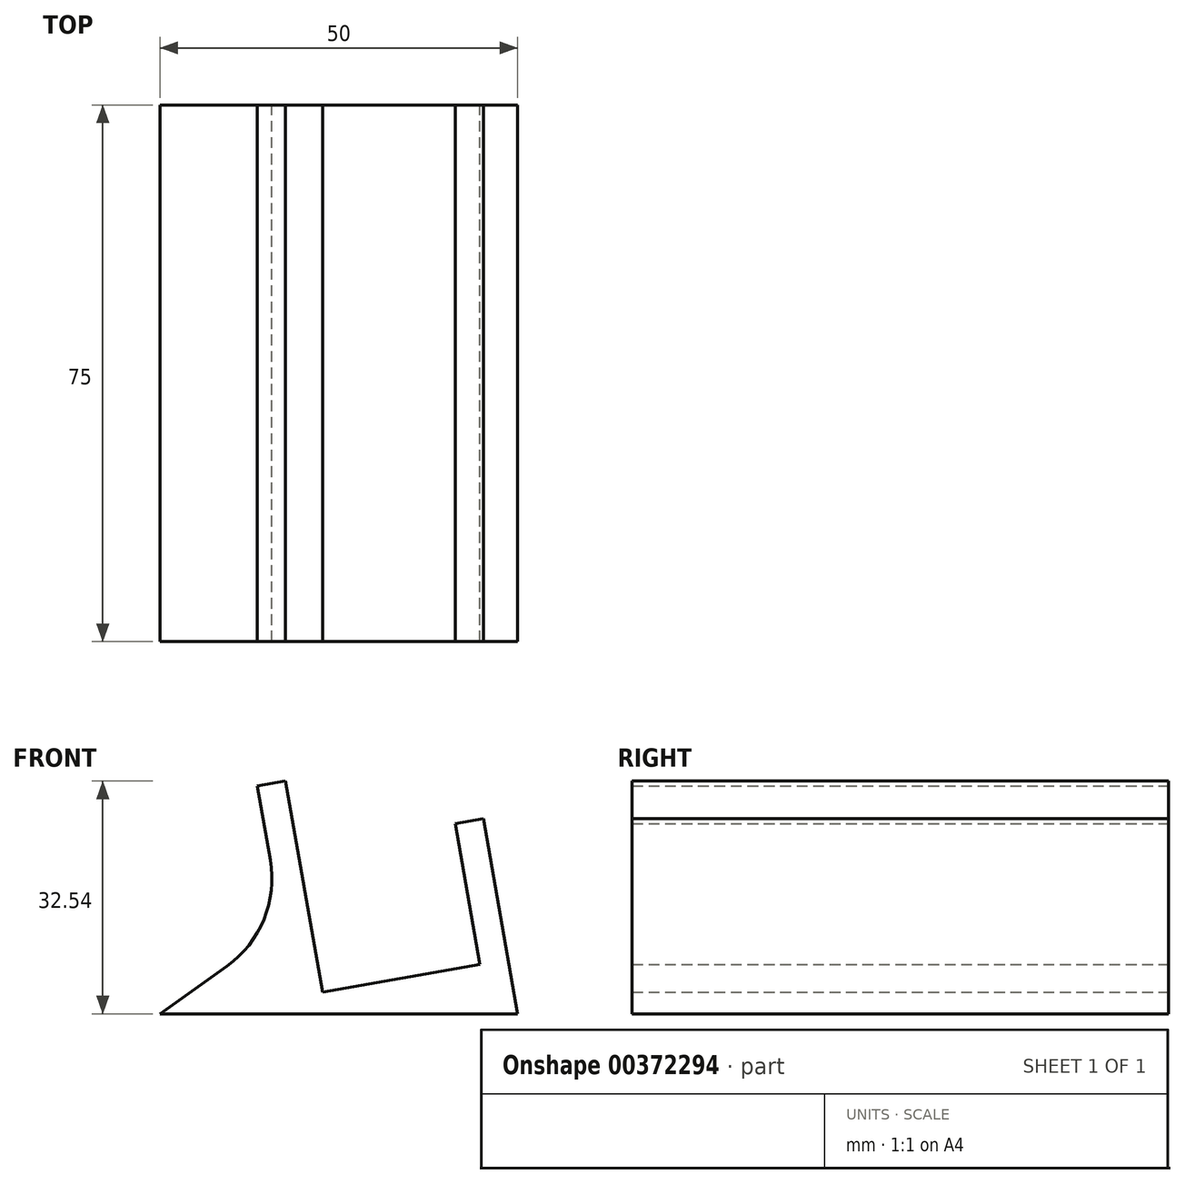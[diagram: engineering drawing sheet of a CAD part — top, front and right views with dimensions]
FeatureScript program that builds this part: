
annotation { "Feature Type Name" : "Feature", "Feature Type Description" : "" }
export const myFeature = defineFeature(function(context is Context, id is Id, definition is map)
    precondition{}
    {
        {
            var Q0;
            Q0=qCreatedBy(makeId("Front.planeOp"),FACE);
            var sketch = newSketch(context, id + "F0", { "sketchPlane" : qUnion([Q0])});
            skLineSegment(sketch, "E0", {"start": v(0, 0) * mm, "end": v(22, 3.88) * mm});
            skLineSegment(sketch, "E1", {"start": v(0, 0) * mm, "end": v(-5.2, 29.54) * mm});
            skLineSegment(sketch, "E2", {"start": v(22, 3.88) * mm, "end": v(18.53, 23.58) * mm});
            skLineSegment(sketch, "E3", {"start": v(18.53, 23.58) * mm, "end": v(22.47, 24.27) * mm});
            skLineSegment(sketch, "E4", {"start": v(-5.2, 29.54) * mm, "end": v(-9.15, 28.85) * mm});
            skLineSegment(sketch, "E5", {"start": v(22.47, 24.27) * mm, "end": v(27.27, -3) * mm});
            skLineSegment(sketch, "E6", {"start": v(27.27, -3) * mm, "end": v(-22.73, -3) * mm});
            skLineSegment(sketch, "E7", {"start": v(-9.15, 28.85) * mm, "end": v(-7.32, 18.48) * mm});
            skLineSegment(sketch, "E8", {"start": v(-13.39, 3.66) * mm, "end": v(-22.73, -3) * mm});
            skPoint(sketch, "E9.visualSharp", {"position": v(-5.68, 9.15) * mm});
            skArc(sketch, "E9.filletArc", {"start": v(-13.39, 3.66) * mm, "mid": v(-8.2, 10.2) * mm, "end": v(-7.32, 18.48) * mm});
            skSolve(sketch);
        }
        {
            var Q0;
            Q0 = qSketchRegion(id + "F0", true);
            extrude(context, id + "F1", {"entities" : qUnion([Q0]), "depth" : 75 * mm, "offsetDistance" : 25 * mm});
        }
    });
